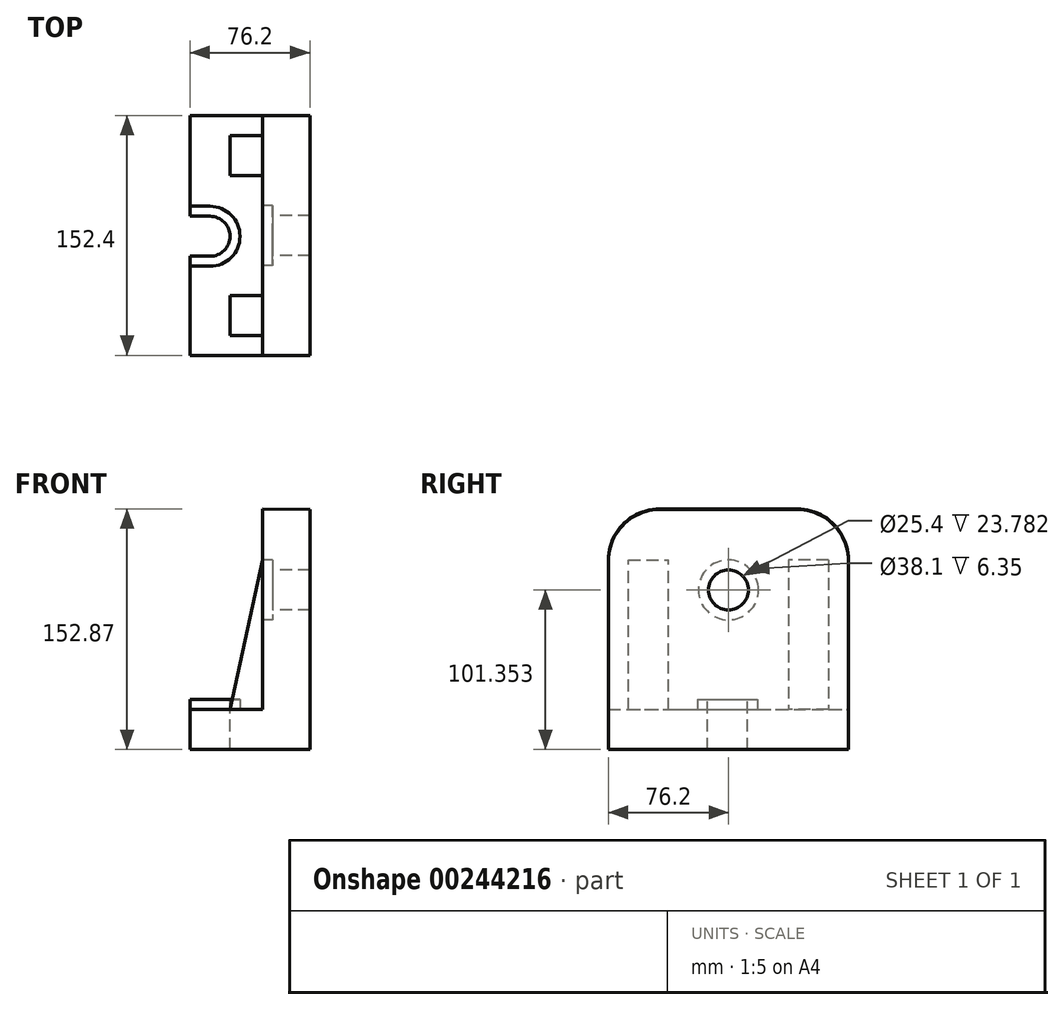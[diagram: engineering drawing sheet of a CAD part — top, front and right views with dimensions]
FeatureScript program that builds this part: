
annotation { "Feature Type Name" : "Feature", "Feature Type Description" : "" }
export const myFeature = defineFeature(function(context is Context, id is Id, definition is map)
    precondition{}
    {
        {
            var Q0;
            Q0=qCreatedBy(makeId("Front.planeOp"),FACE);
            var sketch = newSketch(context, id + "F0", { "sketchPlane" : qUnion([Q0])});
            skLineSegment(sketch, "E0", {"start": v(5.15, 95.66) * mm, "end": v(5.15, -56.74) * mm});
            skLineSegment(sketch, "E1", {"start": v(5.15, -56.74) * mm, "end": v(-71.05, -56.74) * mm});
            skLineSegment(sketch, "E2", {"start": v(-71.05, -56.74) * mm, "end": v(-71.05, -31.34) * mm});
            skLineSegment(sketch, "E3", {"start": v(-71.05, -31.34) * mm, "end": v(-24.98, -31.34) * mm});
            skLineSegment(sketch, "E4", {"start": v(-24.98, -31.34) * mm, "end": v(-24.98, 96.13) * mm});
            skLineSegment(sketch, "E5", {"start": v(-24.98, 96.13) * mm, "end": v(5.15, 95.66) * mm});
            skSolve(sketch);
        }
        {
            var Q0;
            Q0=makeQuery(id+"F0.imprint","IMPRINT",FACE,{"disambiguationData":[TD([[makeQuery(id+"F0.imprint","IMPRINT",EDGE,{"derivedFrom":sQuery(id+"F0.wireOp",EDGE,"E0")}),-1.0]])]});
            extrude(context, id + "F1", {"entities" : qUnion([Q0]), "endBound" : BoundingType.SYMMETRIC, "depth" : 152.4 * mm});
        }
        {
            var Q0;
            Q0=makeQuery(id+"F1.opExtrude","SWEPT_FACE",FACE,{"disambiguationData":[OSD([sQuery(id+"F0.wireOp",EDGE,"E3")])]});
            var sketch = newSketch(context, id + "F2", { "sketchPlane" : qUnion([Q0])});
            skLineSegment(sketch, "E6", {"start": v(-71.05, -13.28) * mm, "end": v(-71.05, 12.12) * mm});
            skLineSegment(sketch, "E7", {"start": v(-71.05, 12.12) * mm, "end": v(-58.35, 12.12) * mm});
            skLineSegment(sketch, "E8", {"start": v(-71.05, -13.28) * mm, "end": v(-58.35, -13.28) * mm});
            skArc(sketch, "E9", {"start": v(-58.35, 12.12) * mm, "mid": v(-45.65, -0.58) * mm, "end": v(-58.35, -13.28) * mm});
            skSolve(sketch);
        }
        {
            var Q0;
            Q0=makeQuery(id+"F2.imprint","IMPRINT",FACE,{"disambiguationData":[TD([[makeQuery(id+"F2.imprint","IMPRINT",EDGE,{"derivedFrom":sQuery(id+"F2.wireOp",EDGE,"E6")}),-1.0]])]});
            extrude(context, id + "F3", {"entities" : qUnion([Q0]), "operationType" : NewBodyOperationType.REMOVE, "oppositeDirection" : true, "depth" : 25.4 * mm});
        }
        {
            var Q0;
            Q0=makeQuery(id+"F1.opExtrude","CAP_EDGE",EDGE,{"disambiguationData":[OSD([sQuery(id+"F0.wireOp",EDGE,"E5")])],"isStart":true});
            var Q1;
            Q1=makeQuery(id+"F1.opExtrude","CAP_EDGE",EDGE,{"disambiguationData":[OSD([sQuery(id+"F0.wireOp",EDGE,"E5")])],"isStart":false});
            fillet(context, id + "F4", {"entities" : qUnion([Q0, Q1]), "radius" : 32.5 * mm, "tangentPropagation" : true, "allowEdgeOverflow" : false});
        }
        {
            var Q0;
            Q0=makeQuery(id+"F1.opExtrude","SWEPT_FACE",FACE,{"disambiguationData":[OSD([sQuery(id+"F0.wireOp",EDGE,"E4")])]});
            var sketch = newSketch(context, id + "F5", { "sketchPlane" : qUnion([Q0])});
            skCircle(sketch, "E10", {"center": v(0, 44.61) * mm, "radius": 12.7 * mm});
            skSolve(sketch);
        }
        {
            var Q0;
            {var subQ0=sQuery(id+"F0.wireOp",EDGE,"E4");var subQ1=sQuery(id+"F0.wireOp",EDGE,"E3");Q0=makeQuery(id+"F10.boolean.opBoolean","MERGE",FACE,{"derivedFrom":[makeQuery(id+"F1.opExtrude","CAP_FACE",FACE,{"disambiguationData":[OSD([sQuery(id+"F0.wireOp",EDGE,"E0"),sQuery(id+"F0.wireOp",EDGE,"E1"),sQuery(id+"F0.wireOp",EDGE,"E2"),subQ1,subQ0,sQuery(id+"F0.wireOp",EDGE,"E5")])],"isStart":false}),makeQuery(id+"F10.opExtrude","CAP_FACE",FACE,{"disambiguationData":[OSD([subQ1,subQ0,sQuery(id+"F9.wireOp",EDGE,"E11")])],"isStart":true})]});}
            cPlane(context, id + "F6", {"entities" : qUnion([Q0]), "cplaneType" : CPlaneType.OFFSET, "offset" : 38.1 * mm, "oppositeDirection" : true, "width" : 152.4 * mm, "height" : 152.4 * mm});
        }
        {
            var Q0;
            {var subQ0=sQuery(id+"F0.wireOp",EDGE,"E4");var subQ1=sQuery(id+"F0.wireOp",EDGE,"E3");Q0=makeQuery(id+"F12.boolean.opBoolean","MERGE",FACE,{"derivedFrom":[makeQuery(id+"F1.opExtrude","CAP_FACE",FACE,{"disambiguationData":[OSD([sQuery(id+"F0.wireOp",EDGE,"E0"),sQuery(id+"F0.wireOp",EDGE,"E1"),sQuery(id+"F0.wireOp",EDGE,"E2"),subQ1,subQ0,sQuery(id+"F0.wireOp",EDGE,"E5")])],"isStart":true}),makeQuery(id+"F12.opExtrude","CAP_FACE",FACE,{"disambiguationData":[OSD([subQ1,subQ0,sQuery(id+"F11.wireOp",EDGE,"E15")])],"isStart":true})]});}
            cPlane(context, id + "F7", {"entities" : qUnion([Q0]), "cplaneType" : CPlaneType.OFFSET, "offset" : 38.1 * mm, "oppositeDirection" : true, "width" : 152.4 * mm, "height" : 152.4 * mm});
        }
        {
            var Q0;
            Q0=sQuery(id+"F5.wireOp",VERTEX,"E10.center");
            var Q1;
            Q1=makeQuery(id+"F1.opExtrude","SWEPT_BODY",BODY,{"disambiguationData":[OSD([sQuery(id+"F0.wireOp",EDGE,"E0"),sQuery(id+"F0.wireOp",EDGE,"E1"),sQuery(id+"F0.wireOp",EDGE,"E2"),sQuery(id+"F0.wireOp",EDGE,"E3"),sQuery(id+"F0.wireOp",EDGE,"E4"),sQuery(id+"F0.wireOp",EDGE,"E5")])]});
            hole(context, id + "F8", {"style" : HoleStyle.C_BORE, "endStyle" : HoleEndStyle.THROUGH, "holeDiameter" : 25.4 * mm, "cBoreDiameter" : 38.1 * mm, "cBoreDepth" : 6.35 * mm, "tappedDepth" : 12.7 * mm, "tapClearance" : 3, "locations" : qUnion([Q0]), "scope" : qUnion([Q1])});
        }
        {
            var Q0;
            Q0=qCreatedBy(id+"F6.planeOp",FACE);
            var sketch = newSketch(context, id + "F9", { "sketchPlane" : qUnion([Q0])});
            skLineSegment(sketch, "E11", {"start": v(-24.98, 63.63) * mm, "end": v(-45.65, -31.34) * mm});
            skLineSegment(sketch, "E12", {"start": v(-45.65, -31.34) * mm, "end": v(-71.05, -31.34) * mm});
            skLineSegment(sketch, "E13", {"start": v(-45.65, -31.34) * mm, "end": v(-24.95, -31.34) * mm});
            skLineSegment(sketch, "E14", {"start": v(-24.95, -31.34) * mm, "end": v(-24.98, 63.63) * mm});
            skSolve(sketch);
        }
        {
            var Q0;
            Q0=makeQuery(id+"F9.imprint","IMPRINT",FACE,{"disambiguationData":[TD([[makeQuery(id+"F9.imprint","IMPRINT",EDGE,{"derivedFrom":sQuery(id+"F9.wireOp",EDGE,"AsIte6rz-qnHt-NqLE-uwtf-CCcA30Ny77uk")}),-1.0]])]});
            var Q1;
            {var subQ0=sQuery(id+"F9.wireOp",EDGE,"E11");Q1=makeQuery(id+"F9.imprint","IMPRINT",FACE,{"disambiguationData":[TD([[makeQuery(id+"F9.imprint","IMPRINT",EDGE,{"derivedFrom":subQ0}),1.0]])]});}
            extrude(context, id + "F10", {"entities" : qUnion([Q0, Q1]), "operationType" : NewBodyOperationType.ADD, "depth" : 25.4 * mm});
        }
        {
            var Q0;
            Q0=qCreatedBy(id+"F7.planeOp",FACE);
            var sketch = newSketch(context, id + "F11", { "sketchPlane" : qUnion([Q0])});
            skLineSegment(sketch, "E15", {"start": v(24.98, 63.63) * mm, "end": v(45.65, -31.34) * mm});
            skLineSegment(sketch, "E16", {"start": v(45.65, -31.34) * mm, "end": v(71.05, -31.34) * mm});
            skLineSegment(sketch, "E17", {"start": v(24.98, 63.63) * mm, "end": v(24.98, -31.34) * mm});
            skLineSegment(sketch, "E18", {"start": v(24.98, -31.34) * mm, "end": v(45.65, -31.34) * mm});
            skSolve(sketch);
        }
        {
            var Q0;
            Q0=makeQuery(id+"F11.imprint","IMPRINT",FACE,{"disambiguationData":[TD([[makeQuery(id+"F11.imprint","IMPRINT",EDGE,{"derivedFrom":sQuery(id+"F11.wireOp",EDGE,"CaLzMBqW-xshu-wiMk-fHWy-mvqrcCZHBJM3")}),-1.0]])]});
            var Q1;
            {var subQ0=sQuery(id+"F11.wireOp",EDGE,"E15");Q1=makeQuery(id+"F11.imprint","IMPRINT",FACE,{"disambiguationData":[TD([[makeQuery(id+"F11.imprint","IMPRINT",EDGE,{"derivedFrom":subQ0}),-1.0]])]});}
            extrude(context, id + "F12", {"entities" : qUnion([Q0, Q1]), "operationType" : NewBodyOperationType.ADD, "depth" : 25.4 * mm});
        }
        {
            var Q0;
            Q0=makeQuery(id+"F1.opExtrude","SWEPT_FACE",FACE,{"disambiguationData":[OSD([sQuery(id+"F0.wireOp",EDGE,"E3")])]});
            var sketch = newSketch(context, id + "F13", { "sketchPlane" : qUnion([Q0])});
            skLineSegment(sketch, "E19", {"start": v(-71.05, 12.12) * mm, "end": v(-58.35, 12.12) * mm});
            skLineSegment(sketch, "E20", {"start": v(-71.05, -13.28) * mm, "end": v(-58.35, -13.28) * mm});
            skLineSegment(sketch, "E21", {"start": v(-71.05, 12.12) * mm, "end": v(-71.05, 18.47) * mm});
            skLineSegment(sketch, "E22", {"start": v(-71.05, -13.28) * mm, "end": v(-71.05, -19.63) * mm});
            skLineSegment(sketch, "E23", {"start": v(-71.05, 18.47) * mm, "end": v(-58.35, 18.47) * mm});
            skLineSegment(sketch, "E24", {"start": v(-71.05, -19.63) * mm, "end": v(-58.35, -19.63) * mm});
            skArc(sketch, "E25", {"start": v(-58.35, 18.47) * mm, "mid": v(-39.3, -0.58) * mm, "end": v(-58.35, -19.63) * mm});
            skArc(sketch, "E26", {"start": v(-58.35, -13.28) * mm, "mid": v(-45.65, -0.58) * mm, "end": v(-58.35, 12.12) * mm});
            skSolve(sketch);
        }
        {
            var Q0;
            Q0=makeQuery(id+"F13.imprint","IMPRINT",FACE,{"disambiguationData":[TD([[makeQuery(id+"F13.imprint","IMPRINT",EDGE,{"derivedFrom":sQuery(id+"F13.wireOp",EDGE,"E19")}),1.0]])]});
            extrude(context, id + "F14", {"entities" : qUnion([Q0]), "operationType" : NewBodyOperationType.ADD, "depth" : 6.35 * mm});
        }
    });
